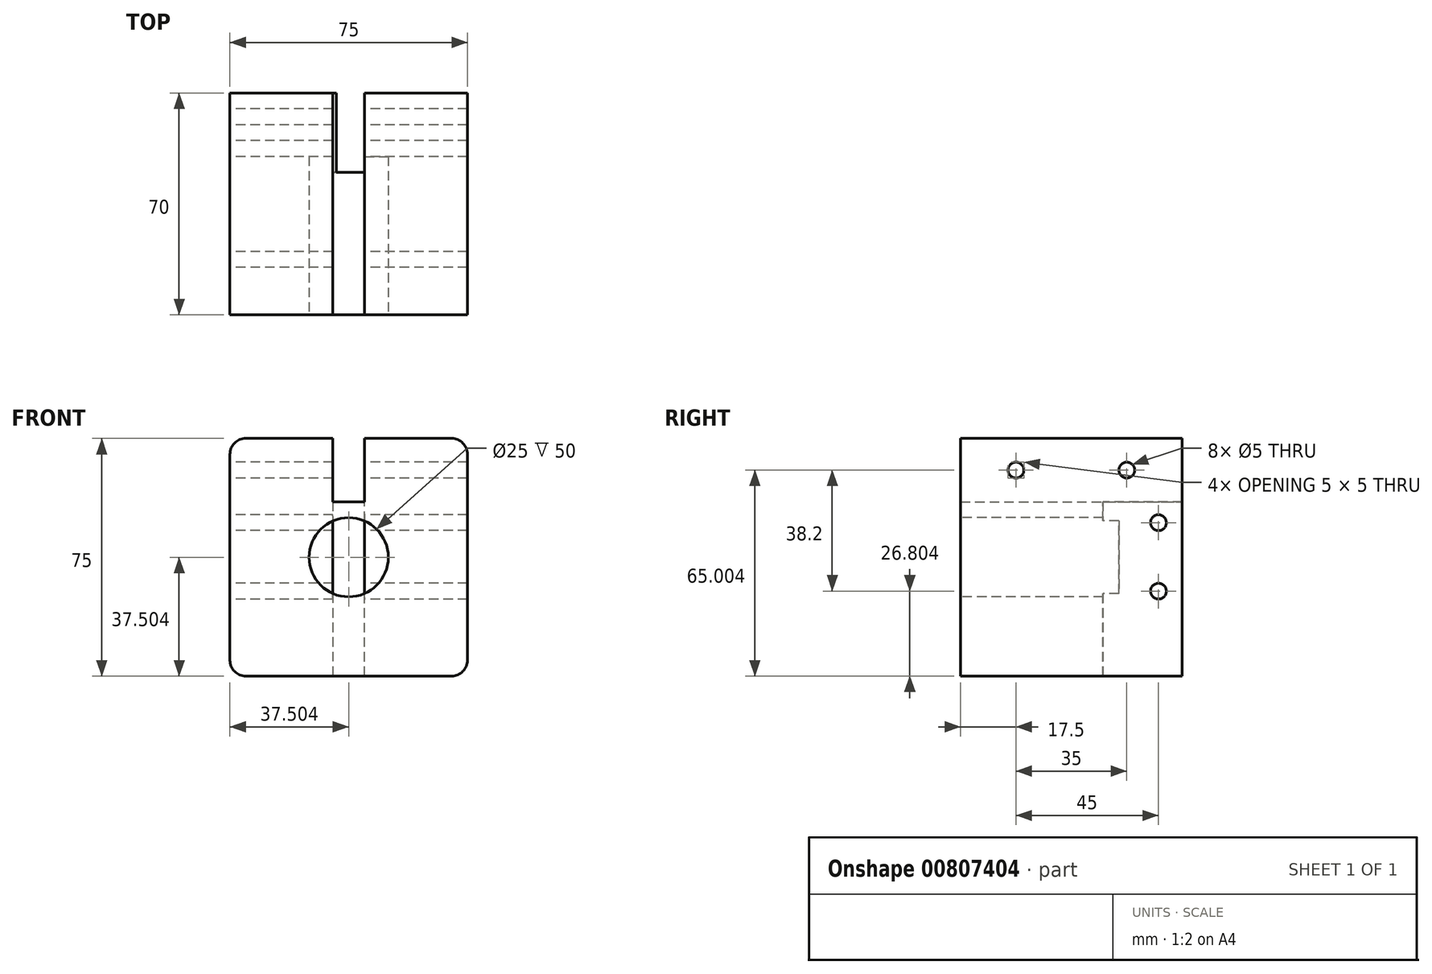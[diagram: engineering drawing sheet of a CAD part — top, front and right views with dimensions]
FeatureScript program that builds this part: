
annotation { "Feature Type Name" : "Feature", "Feature Type Description" : "" }
export const myFeature = defineFeature(function(context is Context, id is Id, definition is map)
    precondition{}
    {
        {
            var Q0;
            Q0=qCreatedBy(makeId("Front.planeOp"),FACE);
            var sketch = newSketch(context, id + "F0", { "sketchPlane" : qUnion([Q0])});
            skLineSegment(sketch, "E0.bottom", {"start": v(-29.62, 20.44) * mm, "end": v(45.38, 20.44) * mm});
            skLineSegment(sketch, "E0.top", {"start": v(-29.62, -54.56) * mm, "end": v(45.38, -54.56) * mm});
            skLineSegment(sketch, "E0.left", {"start": v(-29.62, 20.44) * mm, "end": v(-29.62, -54.56) * mm});
            skLineSegment(sketch, "E0.right", {"start": v(45.38, 20.44) * mm, "end": v(45.38, -54.56) * mm});
            skSolve(sketch);
        }
        {
            var Q0;
            Q0 = qSketchRegion(id + "F0", true);
            extrude(context, id + "F1", {"entities" : qUnion([Q0]), "depth" : 45 * mm, "offsetDistance" : 25 * mm});
        }
        {
            var Q0;
            Q0=makeQuery(id+"F1.opExtrude","SWEPT_EDGE",EDGE,{"disambiguationData":[OSD([sQuery(id+"F0.wireOp",EDGE,"E0.bottom"),sQuery(id+"F0.wireOp",EDGE,"E0.left")])]});
            var Q1;
            Q1=makeQuery(id+"F1.opExtrude","SWEPT_EDGE",EDGE,{"disambiguationData":[OSD([sQuery(id+"F0.wireOp",EDGE,"E0.top"),sQuery(id+"F0.wireOp",EDGE,"E0.left")])]});
            var Q2;
            Q2=makeQuery(id+"F1.opExtrude","SWEPT_EDGE",EDGE,{"disambiguationData":[OSD([sQuery(id+"F0.wireOp",EDGE,"E0.top"),sQuery(id+"F0.wireOp",EDGE,"E0.right")])]});
            var Q3;
            Q3=makeQuery(id+"F1.opExtrude","SWEPT_EDGE",EDGE,{"disambiguationData":[OSD([sQuery(id+"F0.wireOp",EDGE,"E0.bottom"),sQuery(id+"F0.wireOp",EDGE,"E0.right")])]});
            fillet(context, id + "F2", {"entities" : qUnion([Q0, Q1, Q2, Q3]), "radius" : 5 * mm, "tangentPropagation" : true, "allowEdgeOverflow" : false});
        }
        {
            var Q0;
            Q0=makeQuery(id+"F1.opExtrude","CAP_FACE",FACE,{"disambiguationData":[OSD([sQuery(id+"F0.wireOp",EDGE,"E0.bottom"),sQuery(id+"F0.wireOp",EDGE,"E0.top"),sQuery(id+"F0.wireOp",EDGE,"E0.left"),sQuery(id+"F0.wireOp",EDGE,"E0.right")])],"isStart":false});
            var sketch = newSketch(context, id + "F3", { "sketchPlane" : qUnion([Q0])});
            skCircle(sketch, "E1", {"center": v(7.88, -17.06) * mm, "radius": 12.5 * mm});
            skPoint(sketch, "E1.centerSnap0", {"position": v(7.88, 20.44) * mm});
            skPoint(sketch, "E1.centerSnap1", {"position": v(-29.62, -17.06) * mm});
            skSolve(sketch);
        }
        {
            var Q0;
            Q0 = qSketchRegion(id + "F3", true);
            extrude(context, id + "F4", {"entities" : qUnion([Q0]), "operationType" : NewBodyOperationType.REMOVE, "oppositeDirection" : true, "depth" : 25 * mm, "offsetDistance" : 25 * mm});
        }
        {
            var Q0;
            Q0=makeQuery(id+"F1.opExtrude","SWEPT_FACE",FACE,{"disambiguationData":[OSD([sQuery(id+"F0.wireOp",EDGE,"E0.bottom")])]});
            var sketch = newSketch(context, id + "F5", { "sketchPlane" : qUnion([Q0])});
            skLineSegment(sketch, "E2", {"start": v(7.88, 0) * mm, "end": v(7.88, -25) * mm});
            skLineSegment(sketch, "E3", {"start": v(7.88, -25) * mm, "end": v(7.88, -45) * mm});
            skLineSegment(sketch, "E4", {"start": v(7.88, -45) * mm, "end": v(2.88, -45) * mm});
            skLineSegment(sketch, "E5", {"start": v(2.88, -45) * mm, "end": v(2.88, 0) * mm});
            skLineSegment(sketch, "E6", {"start": v(2.88, 0) * mm, "end": v(12.88, 0) * mm});
            skLineSegment(sketch, "E7", {"start": v(12.88, 0) * mm, "end": v(12.88, -45) * mm});
            skSolve(sketch);
        }
        {
            var Q0;
            {var subQ1=sQuery(id+"F5.wireOp",EDGE,"E2");Q0=makeQuery(id+"F5.imprint","IMPRINT",FACE,{"disambiguationData":[TD([[makeQuery(id+"F5.imprint","IMPRINT",EDGE,{"derivedFrom":subQ1}),-1.0]])]});}
            var Q1;
            {var subQ3=sQuery(id+"F5.wireOp",EDGE,"E2");Q1=makeQuery(id+"F5.imprint","IMPRINT",FACE,{"disambiguationData":[TD([[makeQuery(id+"F5.imprint","IMPRINT",EDGE,{"derivedFrom":subQ3}),1.0]])]});}
            extrude(context, id + "F6", {"entities" : qUnion([Q0, Q1]), "operationType" : NewBodyOperationType.REMOVE, "oppositeDirection" : true, "depth" : 20 * mm, "offsetDistance" : 25 * mm});
        }
        {
            var Q0;
            Q0=makeQuery(id+"F0.imprint","IMPRINT",FACE,{"disambiguationData":[TD([[makeQuery(id+"F0.imprint","IMPRINT",EDGE,{"derivedFrom":sQuery(id+"F0.wireOp",EDGE,"E0.bottom")}),-1.0]])]});
            var sketch = newSketch(context, id + "F7", { "sketchPlane" : qUnion([Q0])});
            skLineSegment(sketch, "E8", {"start": v(2.87, 0.44) * mm, "end": v(2.87, -54.64) * mm});
            skLineSegment(sketch, "E9", {"start": v(2.87, -54.64) * mm, "end": v(12.87, -54.64) * mm});
            skLineSegment(sketch, "E10", {"start": v(12.87, -54.64) * mm, "end": v(12.87, 0.5) * mm});
            skLineSegment(sketch, "E11", {"start": v(12.87, 0.5) * mm, "end": v(2.87, 0.44) * mm});
            skSolve(sketch);
        }
        {
            var Q0;
            Q0 = qSketchRegion(id + "F7", true);
            extrude(context, id + "F8", {"entities" : qUnion([Q0]), "operationType" : NewBodyOperationType.REMOVE, "depth" : 25 * mm, "offsetDistance" : 25 * mm});
        }
        {
            var Q0;
            Q0=makeQuery(id+"F1.opExtrude","SWEPT_FACE",FACE,{"disambiguationData":[OSD([sQuery(id+"F0.wireOp",EDGE,"E0.left")])]});
            var sketch = newSketch(context, id + "F9", { "sketchPlane" : qUnion([Q0])});
            skLineSegment(sketch, "E12", {"start": v(0, 15.44) * mm, "end": v(0, -6.16) * mm});
            skLineSegment(sketch, "E13", {"start": v(0, -6.16) * mm, "end": v(0, -27.76) * mm});
            skLineSegment(sketch, "E14", {"start": v(0, -27.76) * mm, "end": v(7.5, -27.76) * mm});
            skLineSegment(sketch, "E15", {"start": v(0, -6.16) * mm, "end": v(7.5, -6.16) * mm});
            skCircle(sketch, "E16", {"center": v(7.5, -6.16) * mm, "radius": 2.5 * mm});
            skCircle(sketch, "E17", {"center": v(7.5, -27.76) * mm, "radius": 2.5 * mm});
            skSolve(sketch);
        }
        {
            var Q0;
            Q0 = qSketchRegion(id + "F9", true);
            extrude(context, id + "F10", {"entities" : qUnion([Q0]), "operationType" : NewBodyOperationType.REMOVE, "endBound" : BoundingType.THROUGH_ALL, "oppositeDirection" : true, "depth" : 25 * mm, "offsetDistance" : 25 * mm});
        }
        {
            var Q0;
            Q0=makeQuery(id+"F1.opExtrude","CAP_FACE",FACE,{"disambiguationData":[OSD([sQuery(id+"F0.wireOp",EDGE,"E0.bottom"),sQuery(id+"F0.wireOp",EDGE,"E0.top"),sQuery(id+"F0.wireOp",EDGE,"E0.left"),sQuery(id+"F0.wireOp",EDGE,"E0.right")])],"isStart":false});
            extrude(context, id + "F11", {"entities" : qUnion([Q0]), "operationType" : NewBodyOperationType.ADD, "depth" : 25 * mm, "offsetDistance" : 25 * mm});
        }
        {
            var Q0;
            {var subQ0=sQuery(id+"F0.wireOp",EDGE,"E0.left");Q0=makeQuery(id+"F11.boolean.opBoolean","MERGE",FACE,{"derivedFrom":[makeQuery(id+"F1.opExtrude","SWEPT_FACE",FACE,{"disambiguationData":[OSD([subQ0])]}),makeQuery(id+"F11.opExtrude","SWEPT_FACE",FACE,{"disambiguationData":[OSD([subQ0])]})]});}
            var sketch = newSketch(context, id + "F12", { "sketchPlane" : qUnion([Q0])});
            skLineSegment(sketch, "E18", {"start": v(0, 15.44) * mm, "end": v(35, 15.44) * mm});
            skLineSegment(sketch, "E19", {"start": v(35, 15.44) * mm, "end": v(17.5, 15.44) * mm});
            skLineSegment(sketch, "E20", {"start": v(17.5, 15.44) * mm, "end": v(52.5, 15.44) * mm});
            skLineSegment(sketch, "E21", {"start": v(52.5, 15.44) * mm, "end": v(52.5, 10.44) * mm});
            skLineSegment(sketch, "E22", {"start": v(52.5, 10.44) * mm, "end": v(17.5, 10.44) * mm});
            skCircle(sketch, "E23", {"center": v(17.5, 10.44) * mm, "radius": 2.5 * mm});
            skCircle(sketch, "E24", {"center": v(52.5, 10.44) * mm, "radius": 2.5 * mm});
            skSolve(sketch);
        }
        {
            var Q0;
            Q0 = qSketchRegion(id + "F12", true);
            extrude(context, id + "F13", {"entities" : qUnion([Q0]), "operationType" : NewBodyOperationType.REMOVE, "endBound" : BoundingType.THROUGH_ALL, "oppositeDirection" : true, "depth" : 25 * mm, "offsetDistance" : 25 * mm});
        }
    });
